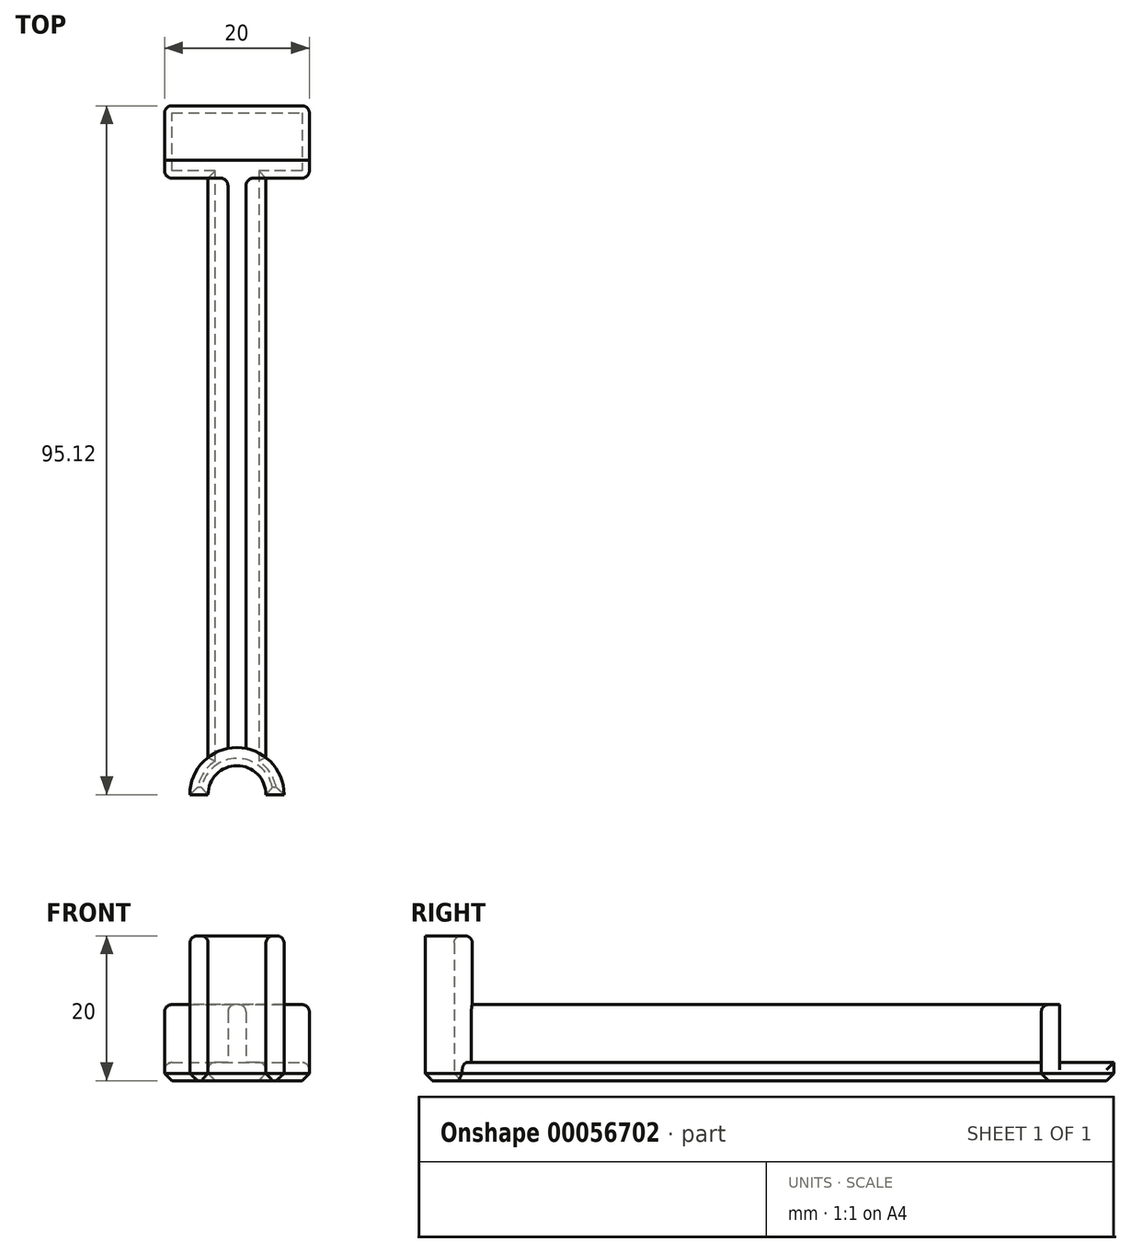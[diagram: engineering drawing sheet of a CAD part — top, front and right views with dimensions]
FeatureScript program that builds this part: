
annotation { "Feature Type Name" : "Feature", "Feature Type Description" : "" }
export const myFeature = defineFeature(function(context is Context, id is Id, definition is map)
    precondition{}
    {
        {
            var Q0;
            Q0=qCreatedBy(makeId("Top.planeOp"),FACE);
            var sketch = newSketch(context, id + "F0", { "sketchPlane" : qUnion([Q0])});
            skCircle(sketch, "E0", {"center": v(0, 0) * mm, "radius": 4 * mm});
            skCircle(sketch, "E1", {"center": v(0, 0) * mm, "radius": 6.5 * mm});
            skLineSegment(sketch, "E2", {"start": v(-6.5, 0) * mm, "end": v(-4, 0) * mm});
            skLineSegment(sketch, "E3", {"start": v(-4, 0) * mm, "end": v(4, 0) * mm});
            skLineSegment(sketch, "E4", {"start": v(4, 0) * mm, "end": v(6.5, 0) * mm});
            skLineSegment(sketch, "E5.rect.bottom", {"start": v(4, 5.12) * mm, "end": v(-4, 5.12) * mm});
            skLineSegment(sketch, "E5.rect.top", {"start": v(4, 85.12) * mm, "end": v(-4, 85.12) * mm});
            skLineSegment(sketch, "E5.rect.left", {"start": v(4, 5.12) * mm, "end": v(4, 85.12) * mm});
            skLineSegment(sketch, "E5.rect.right", {"start": v(-4, 5.12) * mm, "end": v(-4, 85.12) * mm});
            skPoint(sketch, "E5.rect.middle", {"position": v(0, 45.12) * mm});
            skLineSegment(sketch, "E6.rect.bottom", {"start": v(10, 95.12) * mm, "end": v(-10, 95.12) * mm});
            skLineSegment(sketch, "E6.rect.top", {"start": v(10, 85.12) * mm, "end": v(-10, 85.12) * mm});
            skLineSegment(sketch, "E6.rect.left", {"start": v(10, 95.12) * mm, "end": v(10, 85.12) * mm});
            skLineSegment(sketch, "E6.rect.right", {"start": v(-10, 95.12) * mm, "end": v(-10, 85.12) * mm});
            skPoint(sketch, "E6.rect.middle", {"position": v(0, 90.12) * mm});
            skPoint(sketch, "E6.rect.middle.positionSnap0", {"position": v(0, 85.12) * mm});
            skPoint(sketch, "E6.rect.centerSnap0", {"position": v(0, 85.12) * mm});
            skSolve(sketch);
        }
        {
            var Q0;
            {var subQ0=sQuery(id+"F0.wireOp",EDGE,"E2");Q0=makeQuery(id+"F0.imprint","IMPRINT",FACE,{"disambiguationData":[TD([[makeQuery(id+"F0.imprint","IMPRINT",EDGE,{"derivedFrom":subQ0}),1.0]])]});}
            var Q1;
            {var subQ0=sQuery(id+"F0.wireOp",EDGE,"E5.rect.bottom");Q1=makeQuery(id+"F0.imprint","IMPRINT",FACE,{"disambiguationData":[TD([[makeQuery(id+"F0.imprint","IMPRINT",EDGE,{"derivedFrom":subQ0}),-1.0]])]});}
            extrude(context, id + "F1", {"entities" : qUnion([Q0, Q1]), "depth" : 20 * mm});
        }
        {
            var Q0;
            {var subQ0=sQuery(id+"F0.wireOp",EDGE,"E5.rect.left");Q0=makeQuery(id+"F0.imprint","IMPRINT",FACE,{"disambiguationData":[TD([[makeQuery(id+"F0.imprint","IMPRINT",EDGE,{"derivedFrom":subQ0}),1.0]])]});}
            var Q1;
            Q1=makeQuery(id+"F0.imprint","IMPRINT",FACE,{"disambiguationData":[TD([[makeQuery(id+"F0.imprint","IMPRINT",EDGE,{"derivedFrom":sQuery(id+"F0.wireOp",EDGE,"E6.rect.bottom")}),1.0]])]});
            extrude(context, id + "F2", {"entities" : qUnion([Q0, Q1]), "operationType" : NewBodyOperationType.ADD, "depth" : 2.5 * mm});
        }
        {
            var Q0;
            Q0=makeQuery(id+"F2.opExtrude","CAP_FACE",FACE,{"disambiguationData":[OSD([sQuery(id+"F0.wireOp",EDGE,"E1"),sQuery(id+"F0.wireOp",EDGE,"E5.rect.left"),sQuery(id+"F0.wireOp",EDGE,"E5.rect.right"),sQuery(id+"F0.wireOp",EDGE,"E6.rect.bottom"),sQuery(id+"F0.wireOp",EDGE,"E6.rect.top"),sQuery(id+"F0.wireOp",EDGE,"E6.rect.left"),sQuery(id+"F0.wireOp",EDGE,"E6.rect.right")])],"isStart":false});
            var sketch = newSketch(context, id + "F3", { "sketchPlane" : qUnion([Q0])});
            skLineSegment(sketch, "E7.rect.bottom", {"start": v(1.25, 6.38) * mm, "end": v(-1.25, 6.38) * mm});
            skLineSegment(sketch, "E7.rect.top", {"start": v(1.25, 84.19) * mm, "end": v(-1.25, 84.19) * mm});
            skLineSegment(sketch, "E7.rect.left", {"start": v(1.25, 6.38) * mm, "end": v(1.25, 84.19) * mm});
            skLineSegment(sketch, "E7.rect.right", {"start": v(-1.25, 6.38) * mm, "end": v(-1.25, 84.19) * mm});
            skPoint(sketch, "E7.rect.middle", {"position": v(0, 45.28) * mm});
            skLineSegment(sketch, "E8", {"start": v(-10, 87.62) * mm, "end": v(10, 87.62) * mm});
            skLineSegment(sketch, "E9", {"start": v(10, 87.62) * mm, "end": v(10, 85.12) * mm});
            skLineSegment(sketch, "E10", {"start": v(10, 85.12) * mm, "end": v(-10, 85.12) * mm});
            skLineSegment(sketch, "E11", {"start": v(-10, 85.12) * mm, "end": v(-10, 87.62) * mm});
            skLineSegment(sketch, "E12", {"start": v(-1.25, 84.19) * mm, "end": v(-1.25, 85.12) * mm});
            skLineSegment(sketch, "E13", {"start": v(1.25, 84.19) * mm, "end": v(1.25, 85.12) * mm});
            skSolve(sketch);
        }
        {
            var Q0;
            Q0=makeQuery(id+"F3.imprint","IMPRINT",FACE,{"disambiguationData":[TD([[makeQuery(id+"F3.imprint","IMPRINT",EDGE,{"derivedFrom":sQuery(id+"F3.wireOp",EDGE,"E8")}),-1.0]])]});
            var Q1;
            Q1=makeQuery(id+"F3.imprint","IMPRINT",FACE,{"disambiguationData":[TD([[makeQuery(id+"F3.imprint","IMPRINT",EDGE,{"derivedFrom":sQuery(id+"F3.wireOp",EDGE,"E7.rect.top")}),-1.0]])]});
            var Q2;
            Q2=makeQuery(id+"F3.imprint","IMPRINT",FACE,{"disambiguationData":[TD([[makeQuery(id+"F3.imprint","IMPRINT",EDGE,{"derivedFrom":sQuery(id+"F3.wireOp",EDGE,"E7.rect.top")}),1.0]])]});
            extrude(context, id + "F4", {"entities" : qUnion([Q0, Q1, Q2]), "operationType" : NewBodyOperationType.ADD, "depth" : 8 * mm});
        }
        {
            var Q0;
            Q0=makeQuery(id+"F4.opExtrude","CAP_EDGE",EDGE,{"disambiguationData":[OSD([sQuery(id+"F3.wireOp",EDGE,"E8")])],"isStart":true});
            var Q1;
            Q1=makeQuery(id+"F1.opExtrude","CAP_EDGE",EDGE,{"disambiguationData":[OSD([sQuery(id+"F0.wireOp",EDGE,"E1")])],"isStart":false});
            var Q2;
            Q2=makeQuery(id+"F4.opExtrude","CAP_EDGE",EDGE,{"disambiguationData":[OSD([sQuery(id+"F3.wireOp",EDGE,"E7.rect.right"),sQuery(id+"F3.wireOp",EDGE,"E12")])],"isStart":false});
            var Q3;
            Q3=makeQuery(id+"F4.opExtrude","CAP_EDGE",EDGE,{"disambiguationData":[OSD([sQuery(id+"F3.wireOp",EDGE,"E7.rect.left"),sQuery(id+"F3.wireOp",EDGE,"E13")])],"isStart":false});
            var Q4;
            Q4=makeQuery(id+"F4.opExtrude","CAP_EDGE",EDGE,{"disambiguationData":[OSD([sQuery(id+"F3.wireOp",EDGE,"E7.rect.left"),sQuery(id+"F3.wireOp",EDGE,"E13")])],"isStart":true});
            var Q5;
            Q5=makeQuery(id+"F2.opExtrude","CAP_EDGE",EDGE,{"disambiguationData":[OSD([sQuery(id+"F0.wireOp",EDGE,"E5.rect.left")])],"isStart":false});
            var Q6;
            Q6=makeQuery(id+"F4.opExtrude","CAP_EDGE",EDGE,{"disambiguationData":[OSD([sQuery(id+"F3.wireOp",EDGE,"E7.rect.right"),sQuery(id+"F3.wireOp",EDGE,"E12")])],"isStart":true});
            var Q7;
            Q7=makeQuery(id+"F2.opExtrude","CAP_EDGE",EDGE,{"disambiguationData":[OSD([sQuery(id+"F0.wireOp",EDGE,"E5.rect.right")])],"isStart":false});
            var Q8;
            Q8=makeQuery(id+"F1.opExtrude","CAP_EDGE",EDGE,{"disambiguationData":[OSD([sQuery(id+"F0.wireOp",EDGE,"E0")])],"isStart":false});
            var Q9;
            Q9=makeQuery(id+"F2.opExtrude","SWEPT_EDGE",EDGE,{"disambiguationData":[OSD([sQuery(id+"F0.wireOp",EDGE,"E6.rect.bottom"),sQuery(id+"F0.wireOp",EDGE,"E6.rect.right")])]});
            var Q10;
            Q10=makeQuery(id+"F2.opExtrude","SWEPT_EDGE",EDGE,{"disambiguationData":[OSD([sQuery(id+"F0.wireOp",EDGE,"E6.rect.bottom"),sQuery(id+"F0.wireOp",EDGE,"E6.rect.left")])]});
            var Q11;
            Q11=makeQuery(id+"F2.opExtrude","CAP_EDGE",EDGE,{"disambiguationData":[OSD([sQuery(id+"F0.wireOp",EDGE,"E6.rect.right")])],"isStart":false});
            var Q12;
            Q12=makeQuery(id+"F2.opExtrude","CAP_EDGE",EDGE,{"disambiguationData":[OSD([sQuery(id+"F0.wireOp",EDGE,"E6.rect.left")])],"isStart":false});
            var Q13;
            Q13=makeQuery(id+"F4.opExtrude","CAP_EDGE",EDGE,{"disambiguationData":[OSD([sQuery(id+"F3.wireOp",EDGE,"E11")])],"isStart":false});
            var Q14;
            Q14=makeQuery(id+"F4.opExtrude","CAP_EDGE",EDGE,{"disambiguationData":[OSD([sQuery(id+"F3.wireOp",EDGE,"E9")])],"isStart":false});
            var Q15;
            {var subQ0=sQuery(id+"F3.wireOp",EDGE,"E10");var subQ1=makeQuery(id+"F3.imprint","INTERSECT",VERTEX,{"derivedFrom":[makeQuery(id+"F2.opExtrude","CAP_EDGE",EDGE,{"disambiguationData":[OSD([sQuery(id+"F0.wireOp",EDGE,"E5.rect.right")])],"isStart":false}),subQ0]});Q15=makeQuery(id+"F4.opExtrude","CAP_EDGE",EDGE,{"disambiguationData":[OSD([subQ0]),TDD([makeQuery(id+"F3.imprint","IMPRINT",EDGE,{"disambiguationData":[TD([[subQ1,1.0]])],"derivedFrom":subQ0}),makeQuery(id+"F3.imprint","IMPRINT",EDGE,{"disambiguationData":[TD([[subQ1,-1.0]])],"derivedFrom":subQ0})])],"isStart":false});}
            var Q16;
            {var subQ0=sQuery(id+"F3.wireOp",EDGE,"E10");var subQ1=makeQuery(id+"F3.imprint","INTERSECT",VERTEX,{"derivedFrom":[makeQuery(id+"F2.opExtrude","CAP_EDGE",EDGE,{"disambiguationData":[OSD([sQuery(id+"F0.wireOp",EDGE,"E5.rect.left")])],"isStart":false}),subQ0]});Q16=makeQuery(id+"F4.opExtrude","CAP_EDGE",EDGE,{"disambiguationData":[OSD([subQ0]),TDD([makeQuery(id+"F3.imprint","IMPRINT",EDGE,{"disambiguationData":[TD([[subQ1,1.0]])],"derivedFrom":subQ0}),makeQuery(id+"F3.imprint","IMPRINT",EDGE,{"disambiguationData":[TD([[subQ1,-1.0]])],"derivedFrom":subQ0})])],"isStart":false});}
            var Q17;
            Q17=makeQuery(id+"F4.boolean.opBoolean","MERGE",EDGE,{"derivedFrom":[makeQuery(id+"F2.opExtrude","SWEPT_EDGE",EDGE,{"disambiguationData":[OSD([sQuery(id+"F0.wireOp",EDGE,"E6.rect.top"),sQuery(id+"F0.wireOp",EDGE,"E6.rect.right")])]}),makeQuery(id+"F4.opExtrude","SWEPT_EDGE",EDGE,{"disambiguationData":[OSD([sQuery(id+"F3.wireOp",EDGE,"E10"),sQuery(id+"F3.wireOp",EDGE,"E11")])]})]});
            var Q18;
            Q18=makeQuery(id+"F4.opExtrude","SWEPT_EDGE",EDGE,{"disambiguationData":[OSD([sQuery(id+"F3.wireOp",EDGE,"E10"),sQuery(id+"F3.wireOp",EDGE,"E12")])]});
            var Q19;
            Q19=makeQuery(id+"F4.opExtrude","SWEPT_EDGE",EDGE,{"disambiguationData":[OSD([sQuery(id+"F3.wireOp",EDGE,"E10"),sQuery(id+"F3.wireOp",EDGE,"E13")])]});
            var Q20;
            Q20=makeQuery(id+"F4.boolean.opBoolean","MERGE",EDGE,{"derivedFrom":[makeQuery(id+"F2.opExtrude","SWEPT_EDGE",EDGE,{"disambiguationData":[OSD([sQuery(id+"F0.wireOp",EDGE,"E6.rect.top"),sQuery(id+"F0.wireOp",EDGE,"E6.rect.left")])]}),makeQuery(id+"F4.opExtrude","SWEPT_EDGE",EDGE,{"disambiguationData":[OSD([sQuery(id+"F3.wireOp",EDGE,"E9"),sQuery(id+"F3.wireOp",EDGE,"E10")])]})]});
            fillet(context, id + "F5", {"entities" : qUnion([Q0, Q1, Q2, Q3, Q4, Q5, Q6, Q7, Q8, Q9, Q10, Q11, Q12, Q13, Q14, Q15, Q16, Q17, Q18, Q19, Q20]), "radius" : 1 * mm, "tangentPropagation" : true, "allowEdgeOverflow" : false});
        }
        {
            var Q0;
            {var subQ0=sQuery(id+"F0.wireOp",EDGE,"E1");Q0=makeQuery(id+"F2.boolean.opBoolean","MERGE",FACE,{"derivedFrom":[makeQuery(id+"F1.opExtrude","CAP_FACE",FACE,{"disambiguationData":[OSD([sQuery(id+"F0.wireOp",EDGE,"E0"),subQ0,sQuery(id+"F0.wireOp",EDGE,"E2"),sQuery(id+"F0.wireOp",EDGE,"E4")])],"isStart":true}),makeQuery(id+"F2.opExtrude","CAP_FACE",FACE,{"disambiguationData":[OSD([subQ0,sQuery(id+"F0.wireOp",EDGE,"E5.rect.left"),sQuery(id+"F0.wireOp",EDGE,"E5.rect.right"),sQuery(id+"F0.wireOp",EDGE,"E6.rect.bottom"),sQuery(id+"F0.wireOp",EDGE,"E6.rect.top"),sQuery(id+"F0.wireOp",EDGE,"E6.rect.left"),sQuery(id+"F0.wireOp",EDGE,"E6.rect.right")])],"isStart":true})]});}
            chamfer(context, id + "F6", {"entities" : qUnion([Q0]), "width" : 1 * mm, "tangentPropagation" : true});
        }
    });
